FCSTD DOCUMENT  (FreeCAD 0.15R4671 (Git))
Label: Chassis_marco_derivative
License: All rights reserved
LicenseURL: http://en.wikipedia.org/wiki/All_rights_reserved
objects: Sketcher::SketchObject×1
note: 1 computed .brp shape members not serialized (recipe doc carries the construction recipe); baked Part::Feature solids carry a one-line shape summary decoded from their .brp

FEATURE [Sketcher::SketchObject] Sketch
  sketch-geometry (29):
    g0: LineSegment StartX=-104.283 StartY=35 StartZ=0 EndX=-85 EndY=35 EndZ=0
    g1: LineSegment StartX=-85 StartY=35 StartZ=0 EndX=-85 EndY=-35 EndZ=0
    g2: LineSegment StartX=-85 StartY=-35 StartZ=0 EndX=-104.283 EndY=-35 EndZ=0
    g3: LineSegment StartX=104.283 StartY=35 StartZ=0 EndX=85 EndY=35 EndZ=0
    g4: LineSegment StartX=85 StartY=35 StartZ=0 EndX=85 EndY=-35 EndZ=0
    g5: LineSegment StartX=85 StartY=-35 StartZ=0 EndX=104.283 EndY=-35 EndZ=0
    g6: Circle CenterX=-75.5 CenterY=10.85 CenterZ=0 NormalX=0 NormalY=0 NormalZ=1 Radius=1.5
    g7: Circle CenterX=-75.5 CenterY=-10.85 CenterZ=0 NormalX=0 NormalY=0 NormalZ=1 Radius=1.5
    g8: Circle CenterX=-43.75 CenterY=10.85 CenterZ=0 NormalX=0 NormalY=0 NormalZ=1 Radius=1.5
    g9: Circle CenterX=-43.75 CenterY=-10.85 CenterZ=0 NormalX=0 NormalY=0 NormalZ=1 Radius=1.5
    g10: Circle CenterX=43.75 CenterY=-10.85 CenterZ=0 NormalX=0 NormalY=0 NormalZ=1 Radius=1.5
    g11: Circle CenterX=43.75 CenterY=10.85 CenterZ=0 NormalX=0 NormalY=0 NormalZ=1 Radius=1.5
    g12: Circle CenterX=75.5 CenterY=10.85 CenterZ=0 NormalX=0 NormalY=0 NormalZ=1 Radius=1.5
    g13: Circle CenterX=75.5 CenterY=-10.85 CenterZ=0 NormalX=0 NormalY=0 NormalZ=1 Radius=1.5
    g14: Circle CenterX=-7.366 CenterY=-100 CenterZ=0 NormalX=0 NormalY=0 NormalZ=1 Radius=1.15
    g15: Circle CenterX=7.366 CenterY=-100 CenterZ=0 NormalX=0 NormalY=0 NormalZ=1 Radius=1.15
    g16: Circle CenterX=-7.366 CenterY=100 CenterZ=0 NormalX=0 NormalY=0 NormalZ=1 Radius=1.15
    g17: Circle CenterX=7.366 CenterY=100 CenterZ=0 NormalX=0 NormalY=0 NormalZ=1 Radius=1.15
    g18: ArcOfCircle CenterX=0 CenterY=0 CenterZ=0 NormalX=0 NormalY=0 NormalZ=1 Radius=110 StartAngle=0.323811 EndAngle=2.81778
    g19: ArcOfCircle CenterX=0 CenterY=0 CenterZ=0 NormalX=0 NormalY=0 NormalZ=1 Radius=110 StartAngle=0.323811 EndAngle=2.81778
    g20: ArcOfCircle CenterX=0 CenterY=0 CenterZ=0 NormalX=0 NormalY=0 NormalZ=1 Radius=110 StartAngle=3.4654 EndAngle=5.95937
    g21: LineSegment [constr] StartX=-75.5 StartY=10.85 StartZ=0 EndX=-43.75 EndY=10.85 EndZ=0
    g22: LineSegment [constr] StartX=-43.75 StartY=10.85 StartZ=0 EndX=-43.75 EndY=-10.85 EndZ=0
    g23: LineSegment [constr] StartX=-43.75 StartY=-10.85 StartZ=0 EndX=-75.5 EndY=-10.85 EndZ=0
    g24: LineSegment [constr] StartX=-75.5 StartY=-10.85 StartZ=0 EndX=-75.5 EndY=10.85 EndZ=0
    g25: LineSegment [constr] StartX=7.366 StartY=100 StartZ=0 EndX=-7.366 EndY=100 EndZ=0
    g26: LineSegment [constr] StartX=-7.366 StartY=100 StartZ=0 EndX=-7.366 EndY=-100 EndZ=0
    g27: LineSegment [constr] StartX=-7.366 StartY=-100 StartZ=0 EndX=7.366 EndY=-100 EndZ=0
    g28: LineSegment [constr] StartX=7.366 StartY=-100 StartZ=0 EndX=7.366 EndY=100 EndZ=0
  constraints (75):
    c: Coincident(g0,g1)
    c: Vertical(g1)
    c: Coincident(g1,g2)
    c: Horizontal(g2)
    c: Parallel(g0,g2)
    c: Symmetric(g0,g1,g-1)
    c: DistanceX(g-2,g0) = -85
    c: Distance(g0,g1) = 70
    c: Horizontal(g3)
    c: Coincident(g3,g4)
    c: Vertical(g4)
    c: Coincident(g4,g5)
    c: Horizontal(g5)
    c: Distance(g3,g4) = 70
    c: Symmetric(g3,g4,g-1)
    c: Symmetric(g6,g7,g-1)
    c: Symmetric(g8,g9,g-1)
    c: Symmetric(g11,g10,g-1)
    c: Symmetric(g12,g13,g-1)
    c: Symmetric(g8,g11,g-2)
    c: Symmetric(g7,g13,g-2)
    c: Symmetric(g0,g3,g-2)
    c: Coincident(g18,g-1)
    c: Coincident(g18,g3)
    c: Coincident(g18,g0)
    c: Radius(g19) = 110
    c: Coincident(g19,g-1)
    c: Coincident(g19,g0)
    c: Coincident(g19,g3)
    c: Radius(g20) = 110
    c: Coincident(g20,g-1)
    c: Coincident(g20,g5)
    c: Coincident(g20,g2)
    c: Coincident(g21,g22)
    c: Coincident(g22,g23)
    c: Coincident(g23,g24)
    c: Coincident(g24,g21)
    c: Horizontal(g21)
    c: Horizontal(g23)
    c: Vertical(g22)
    c: Vertical(g24)
    c: Coincident(g21,g8)
    c: Coincident(g21,g6)
    c: Coincident(g23,g7)
    c: Radius(g17) = 1.15
    c: DistanceY(g24) = 21.7
    c: DistanceX(g21) = 31.75
    c: DistanceX(g6,g0) = -9.5
    c: Coincident(g25,g26)
    c: Coincident(g26,g27)
    c: Coincident(g27,g28)
    c: Coincident(g28,g25)
    c: Horizontal(g25)
    c: Horizontal(g27)
    c: Vertical(g26)
    c: Vertical(g28)
    c: DistanceY(g28) = 200
    c: Coincident(g25,g16)
    c: DistanceX(g25) = -14.732
    c: Coincident(g17,g25)
    c: Coincident(g14,g26)
    c: Coincident(g15,g27)
    c: Symmetric(g16,g17,g-2)
    c: Equal(g16,g17)
    c: Equal(g17,g15)
    c: Equal(g15,g14)
    c: Equal(g8,g9)
    c: Equal(g9,g7)
    c: Equal(g7,g6)
    c: Equal(g6,g11)
    c: Equal(g11,g10)
    c: Equal(g10,g12)
    c: Equal(g12,g13)
    c: Radius(g6) = 1.5
    c: Symmetric(g15,g17,g-1)
